# Revit family: Faucet_Single_Control-American_Standard-Pekoe-4332.310
name_source: partatom
category: Plumbing Fixtures
units: mm (PartAtom-declared; Revit-internal decimal feet)

## family parameters
Always vertical = No
Cut with Voids When Loaded = No
OmniClass Number = 23.45.55.14
OmniClass Title = Single Faucets
Part Type = Normal
Room Calculation Point = No
Round Connector Dimension = Use Diameter
Shared = Yes
Work Plane-Based = Yes

## types (2) — shared parameters
ADA Compliant = Yes
Assembly Code = D2020300
CW Connection = Yes
CWFU = 1.5
Default Elevation = 0"
Description = Pekoe Single Control Bar Faucet With Hi-Flow Spout.
HW Connection = Yes
HWFU = 1.5
Height = 10 3/4"
Length = 5 3/4"
Manufacturer = American Standard
Product Documentation Link = https://www.americanstandard-us.com
Product URL = https://www.americanstandard-us.com
Revised Date = 01/27/2017
URL = http://www.americanstandard-us.com
Vent Connection = No
Waste Connection = No
Width = 2"
zero-valued in all types: WFU

## per-type parameters (varying)
| type | Finish | Material |
| 4332.310.002 | Brass-American Standard-002-Polished Chrome | Brass-American Standard-002-Polished Chrome |
| 4332.310.075 | Brass-American Standard-075-Stainless Steel | Brass-American Standard-075-Stainless Steel |

note: column(s) folded — value = type name in every type: Model

## geometry (parser evidence)
native form markers: Sweep x2
no freeform markers — native parametric forms only
